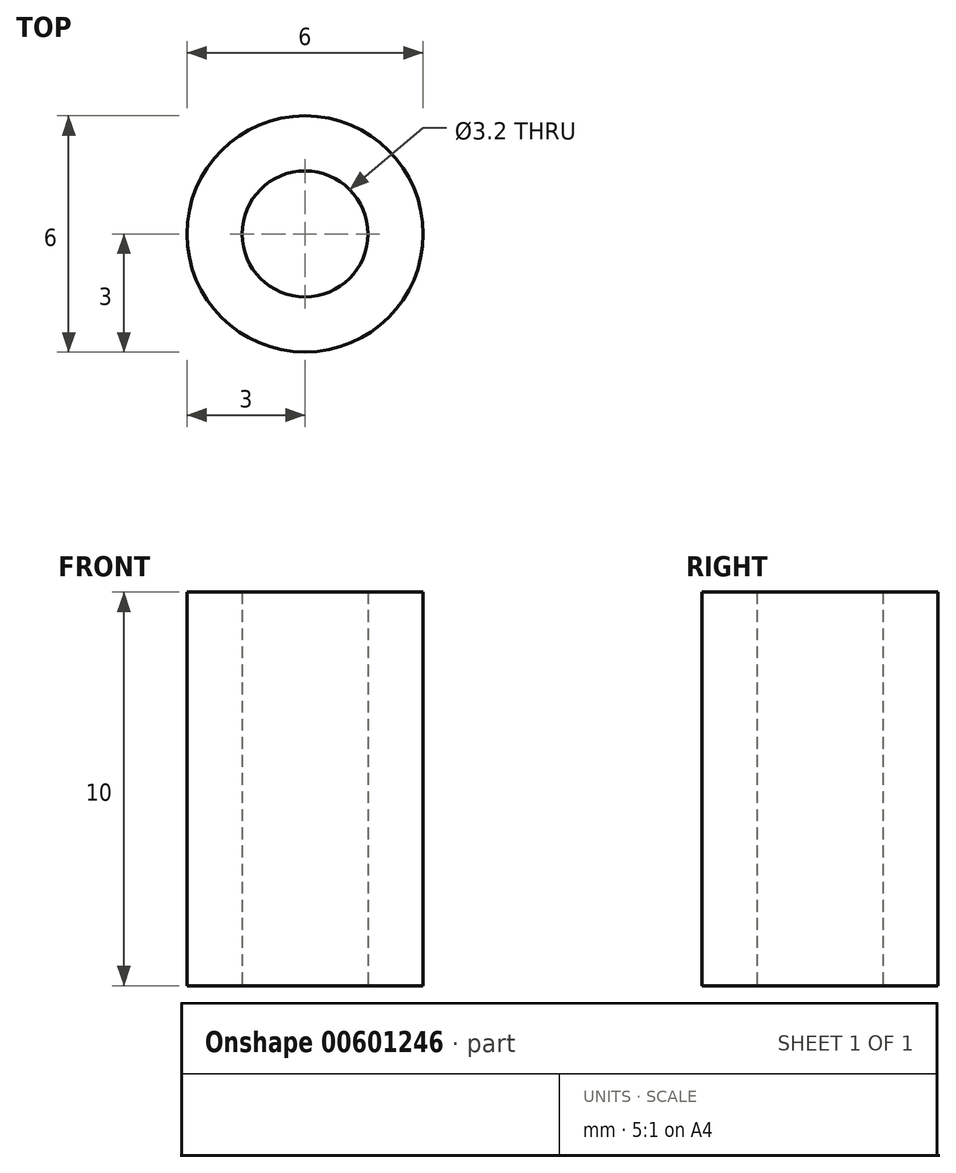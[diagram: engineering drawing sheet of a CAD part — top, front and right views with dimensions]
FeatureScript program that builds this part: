
annotation { "Feature Type Name" : "Feature", "Feature Type Description" : "" }
export const myFeature = defineFeature(function(context is Context, id is Id, definition is map)
    precondition{}
    {
        {
            var Q0;
            Q0=qCreatedBy(makeId("Top.planeOp"),FACE);
            var sketch = newSketch(context, id + "F0", { "sketchPlane" : qUnion([Q0])});
            skCircle(sketch, "E0", {"center": v(0, 0) * mm, "radius": 3 * mm});
            skCircle(sketch, "E1", {"center": v(0, 0) * mm, "radius": 1.6 * mm});
            skSolve(sketch);
        }
        {
            var Q0;
            Q0=makeQuery(id+"F0.imprint","IMPRINT",FACE,{"disambiguationData":[TD([[makeQuery(id+"F0.imprint","IMPRINT",EDGE,{"derivedFrom":sQuery(id+"F0.wireOp",EDGE,"E0")}),1.0]])]});
            extrude(context, id + "F1", {"entities" : qUnion([Q0]), "depth" : 10 * mm, "offsetDistance" : 25 * mm});
        }
    });
